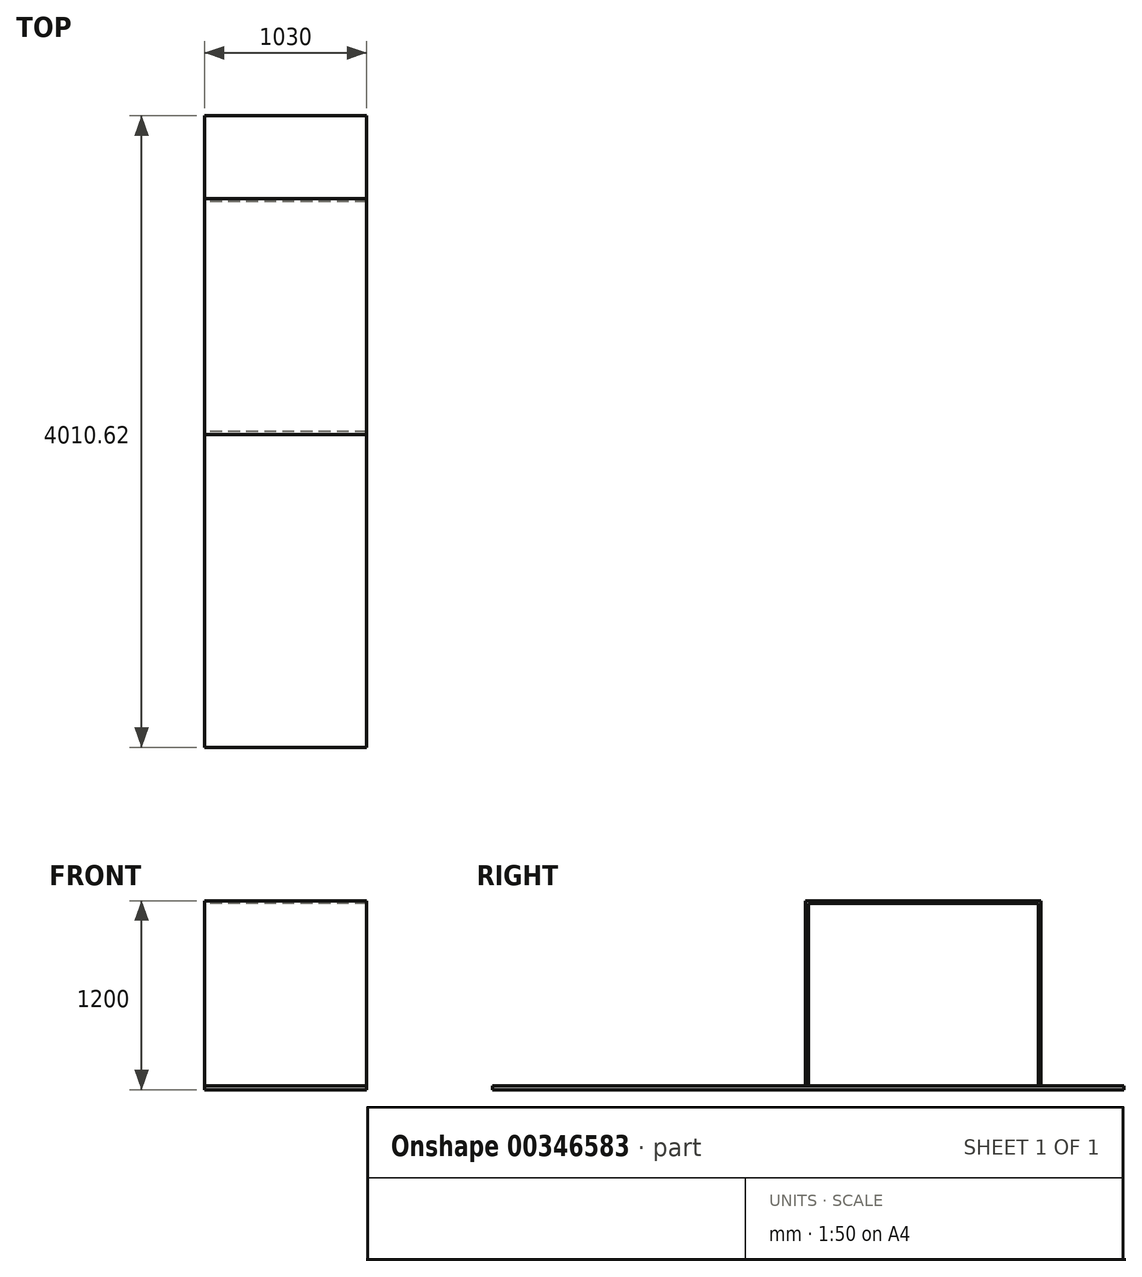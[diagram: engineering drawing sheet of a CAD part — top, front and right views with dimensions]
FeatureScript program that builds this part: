
annotation { "Feature Type Name" : "Feature", "Feature Type Description" : "" }
export const myFeature = defineFeature(function(context is Context, id is Id, definition is map)
    precondition{}
    {
        {
            var Q0;
            Q0=qCreatedBy(makeId("Right.planeOp"),FACE);
            var sketch = newSketch(context, id + "F0", { "sketchPlane" : qUnion([Q0])});
            skLineSegment(sketch, "E0.top", {"start": v(748, 587.5) * mm, "end": v(-748, 587.5) * mm});
            skLineSegment(sketch, "E0.left", {"start": v(748, -587.5) * mm, "end": v(748, 587.5) * mm});
            skLineSegment(sketch, "E0.right", {"start": v(-748, -587.5) * mm, "end": v(-748, 587.5) * mm});
            skPoint(sketch, "E0.middle", {"position": v(0, 0) * mm});
            skLineSegment(sketch, "E1.0", {"start": v(730, 569.5) * mm, "end": v(-730, 569.5) * mm});
            skLineSegment(sketch, "E1.1", {"start": v(730, -587.5) * mm, "end": v(730, 569.5) * mm});
            skLineSegment(sketch, "E1.3", {"start": v(-730, -587.5) * mm, "end": v(-730, 569.5) * mm});
            skLineSegment(sketch, "E2", {"start": v(-748, -587.5) * mm, "end": v(-730, -587.5) * mm});
            skLineSegment(sketch, "E3", {"start": v(730, -587.5) * mm, "end": v(748, -587.5) * mm});
            skSolve(sketch);
        }
        {
            var Q0;
            Q0 = qSketchRegion(id + "F0", true);
            extrude(context, id + "F1", {"entities" : qUnion([Q0]), "depth" : 1030 * mm});
        }
        {
            var Q0;
            Q0=makeQuery(id+"F1.opExtrude","SWEPT_FACE",FACE,{"disambiguationData":[OSD([sQuery(id+"F0.wireOp",EDGE,"E2")])]});
            var sketch = newSketch(context, id + "F2", { "sketchPlane" : qUnion([Q0])});
            skLineSegment(sketch, "E4.bottom", {"start": v(0, -1275.3) * mm, "end": v(1030, -1275.3) * mm});
            skLineSegment(sketch, "E4.top", {"start": v(0, 2735.3) * mm, "end": v(1030, 2735.3) * mm});
            skLineSegment(sketch, "E4.left", {"start": v(0, -1275.3) * mm, "end": v(0, 2735.3) * mm});
            skLineSegment(sketch, "E4.right", {"start": v(1030, -1275.3) * mm, "end": v(1030, 2735.3) * mm});
            skPoint(sketch, "E4.middle", {"position": v(515, 730) * mm});
            skSolve(sketch);
        }
        {
            var Q0;
            Q0 = qSketchRegion(id + "F2", true);
            extrude(context, id + "F3", {"entities" : qUnion([Q0]), "depth" : 25 * mm});
        }
    });
